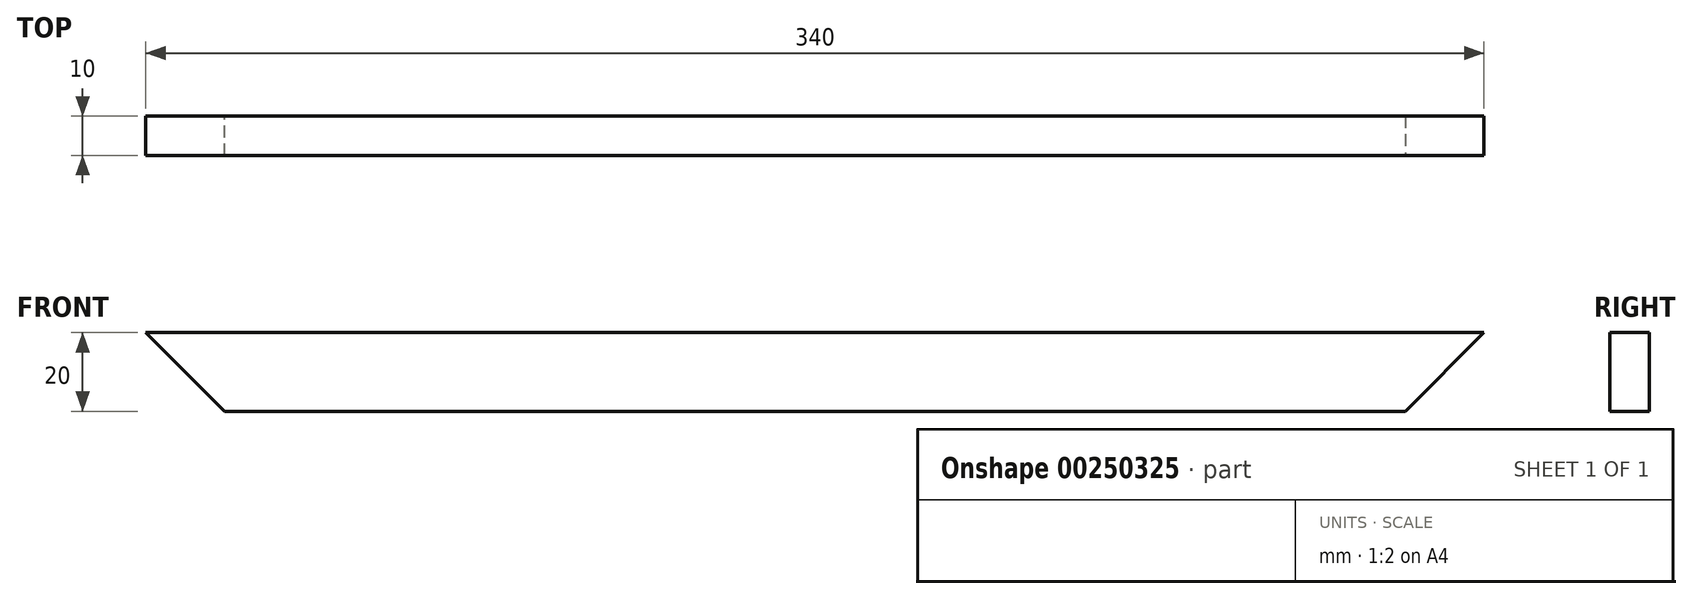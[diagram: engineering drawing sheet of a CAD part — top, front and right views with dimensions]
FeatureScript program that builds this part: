
annotation { "Feature Type Name" : "Feature", "Feature Type Description" : "" }
export const myFeature = defineFeature(function(context is Context, id is Id, definition is map)
    precondition{}
    {
        {
            var Q0;
            Q0=qCreatedBy(makeId("Front.planeOp"),FACE);
            var sketch = newSketch(context, id + "F0", { "sketchPlane" : qUnion([Q0])});
            skLineSegment(sketch, "E0.bottom", {"start": v(279.62, 47.38) * mm, "end": v(-60.38, 47.38) * mm});
            skLineSegment(sketch, "E0.top", {"start": v(279.62, 27.38) * mm, "end": v(-60.38, 27.38) * mm});
            skLineSegment(sketch, "E0.left", {"start": v(279.62, 47.38) * mm, "end": v(279.62, 27.38) * mm});
            skLineSegment(sketch, "E0.right", {"start": v(-60.38, 47.38) * mm, "end": v(-60.38, 27.38) * mm});
            skSolve(sketch);
        }
        {
            var Q0;
            Q0=makeQuery(id+"F0.imprint","IMPRINT",FACE,{"disambiguationData":[TD([[makeQuery(id+"F0.imprint","IMPRINT",EDGE,{"derivedFrom":sQuery(id+"F0.wireOp",EDGE,"E0.bottom")}),1.0]])]});
            extrude(context, id + "F1", {"entities" : qUnion([Q0]), "depth" : 10 * mm});
        }
        {
            var Q0;
            Q0=makeQuery(id+"F1.opExtrude","SWEPT_EDGE",EDGE,{"disambiguationData":[OSD([sQuery(id+"F0.wireOp",EDGE,"E0.top"),sQuery(id+"F0.wireOp",EDGE,"E0.right")])]});
            var Q1;
            Q1=makeQuery(id+"F1.opExtrude","SWEPT_EDGE",EDGE,{"disambiguationData":[OSD([sQuery(id+"F0.wireOp",EDGE,"E0.top"),sQuery(id+"F0.wireOp",EDGE,"E0.left")])]});
            chamfer(context, id + "F2", {"entities" : qUnion([Q0, Q1]), "width" : 20 * mm, "tangentPropagation" : true});
        }
    });
